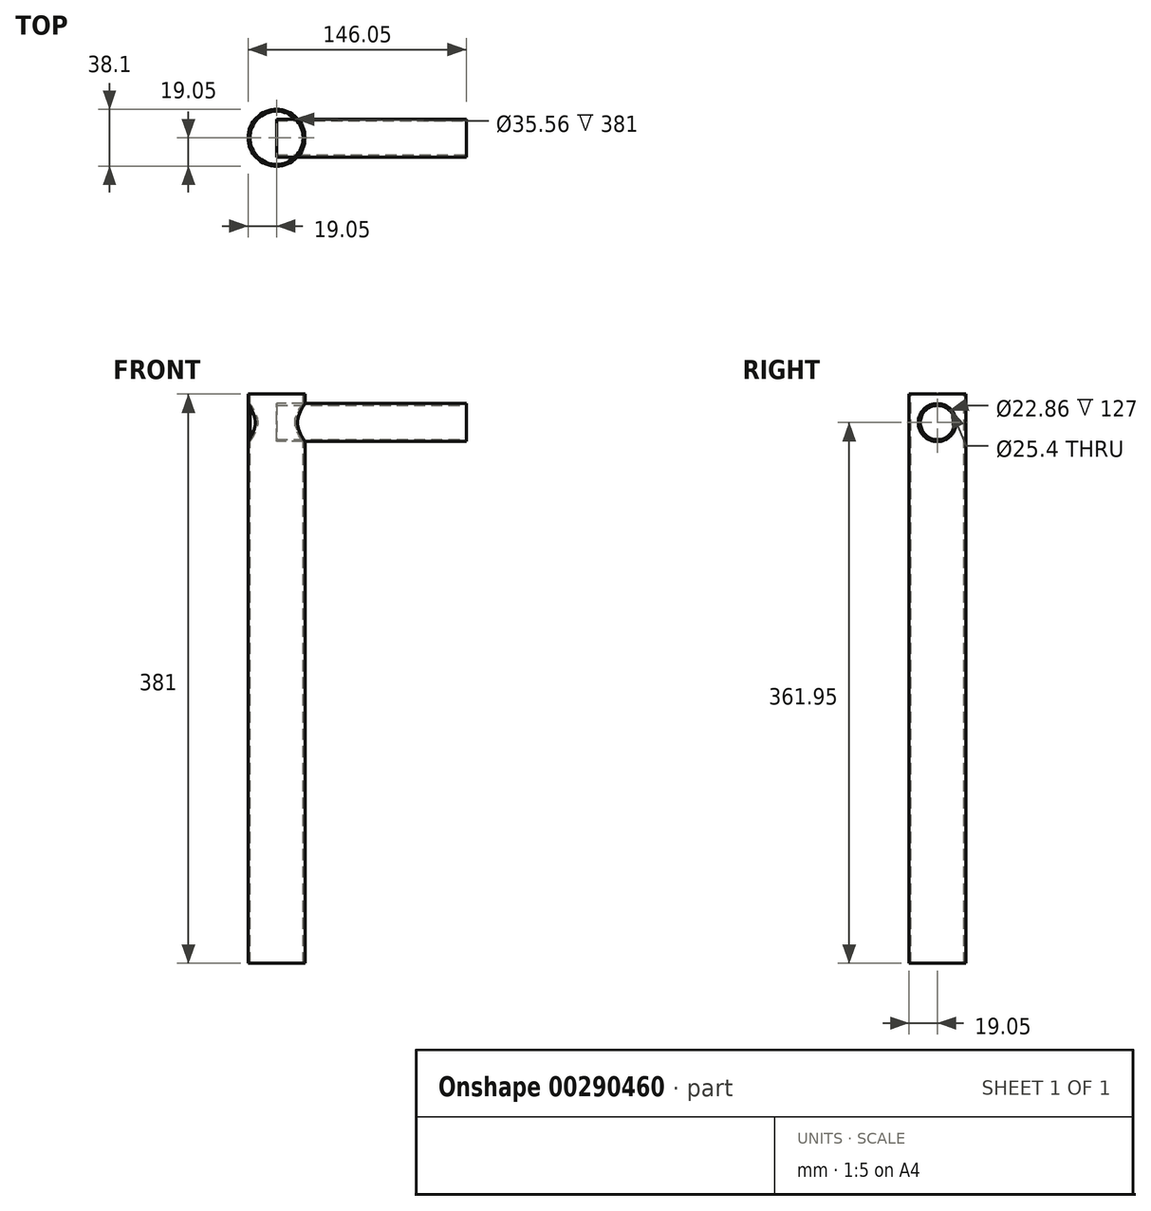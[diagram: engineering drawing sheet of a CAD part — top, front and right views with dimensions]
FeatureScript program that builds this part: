
annotation { "Feature Type Name" : "Feature", "Feature Type Description" : "" }
export const myFeature = defineFeature(function(context is Context, id is Id, definition is map)
    precondition{}
    {
        {
            var Q0;
            Q0=qCreatedBy(makeId("Top.planeOp"),FACE);
            var sketch = newSketch(context, id + "F0", { "sketchPlane" : qUnion([Q0])});
            skCircle(sketch, "E0", {"center": v(0, 0) * mm, "radius": 19.05 * mm});
            skSolve(sketch);
        }
        {
            var Q0;
            Q0 = qSketchRegion(id + "F0", true);
            extrude(context, id + "F1", {"entities" : qUnion([Q0]), "depth" : 381 * mm});
        }
        {
            var Q0;
            Q0=makeQuery(id+"F1.opExtrude","CAP_FACE",FACE,{"disambiguationData":[OSD([sQuery(id+"F0.wireOp",EDGE,"E0")])],"isStart":false});
            var sketch = newSketch(context, id + "F2", { "sketchPlane" : qUnion([Q0])});
            skCircle(sketch, "E1", {"center": v(0, 0) * mm, "radius": 17.78 * mm});
            skSolve(sketch);
        }
        {
            var Q0;
            Q0=makeQuery(id+"F2.imprint","IMPRINT",FACE,{"disambiguationData":[TD([[makeQuery(id+"F2.imprint","IMPRINT",EDGE,{"derivedFrom":sQuery(id+"F2.wireOp",EDGE,"E1")}),1.0]])]});
            extrude(context, id + "F3", {"entities" : qUnion([Q0]), "operationType" : NewBodyOperationType.REMOVE, "oppositeDirection" : true, "depth" : 381 * mm});
        }
        {
            var Q0;
            Q0=qCreatedBy(makeId("Right.planeOp"),FACE);
            var sketch = newSketch(context, id + "F4", { "sketchPlane" : qUnion([Q0])});
            skLineSegment(sketch, "E2", {"start": v(-19.19, 381) * mm, "end": v(-19.19, 342.9) * mm, "construction": true});
            skLineSegment(sketch, "E3", {"start": v(-19.19, 342.9) * mm, "end": v(18.91, 342.9) * mm, "construction": true});
            skLineSegment(sketch, "E4", {"start": v(18.91, 342.9) * mm, "end": v(18.91, 381) * mm, "construction": true});
            skLineSegment(sketch, "E5", {"start": v(18.91, 381) * mm, "end": v(-19.19, 381) * mm, "construction": true});
            skLineSegment(sketch, "E6", {"start": v(-19.19, 361.95) * mm, "end": v(18.91, 361.95) * mm, "construction": true});
            skCircle(sketch, "E7", {"center": v(-0.14, 361.95) * mm, "radius": 12.7 * mm});
            skSolve(sketch);
        }
        {
            var Q0;
            Q0 = qSketchRegion(id + "F4", true);
            extrude(context, id + "F5", {"entities" : qUnion([Q0]), "operationType" : NewBodyOperationType.ADD, "depth" : 127 * mm});
        }
        {
            var Q0;
            Q0=makeQuery(id+"F5.opExtrude","CAP_FACE",FACE,{"disambiguationData":[OSD([sQuery(id+"F4.wireOp",EDGE,"E7")])],"isStart":false});
            var sketch = newSketch(context, id + "F6", { "sketchPlane" : qUnion([Q0])});
            skLineSegment(sketch, "E8", {"start": v(0, 374.65) * mm, "end": v(0, 349.25) * mm, "construction": true});
            skLineSegment(sketch, "E9", {"start": v(0, 349.25) * mm, "end": v(0, 361.95) * mm, "construction": true});
            skLineSegment(sketch, "E10", {"start": v(0, 361.95) * mm, "end": v(12.56, 361.95) * mm, "construction": true});
            skLineSegment(sketch, "E11", {"start": v(12.56, 361.95) * mm, "end": v(-12.84, 361.95) * mm, "construction": true});
            skCircle(sketch, "E12", {"center": v(0, 361.95) * mm, "radius": 11.43 * mm});
            skSolve(sketch);
        }
        {
            var Q0;
            Q0=makeQuery(id+"F6.imprint","IMPRINT",FACE,{"disambiguationData":[TD([[makeQuery(id+"F6.imprint","IMPRINT",EDGE,{"derivedFrom":sQuery(id+"F6.wireOp",EDGE,"E12")}),1.0]])]});
            extrude(context, id + "F7", {"entities" : qUnion([Q0]), "operationType" : NewBodyOperationType.REMOVE, "oppositeDirection" : true, "depth" : 127 * mm});
        }
        {
            var Q0;
            Q0=qCreatedBy(makeId("Right.planeOp"),FACE);
            var sketch = newSketch(context, id + "F8", { "sketchPlane" : qUnion([Q0])});
            skLineSegment(sketch, "E13", {"start": v(19.05, 381) * mm, "end": v(-19.05, 381) * mm, "construction": true});
            skLineSegment(sketch, "E14", {"start": v(-19.05, 381) * mm, "end": v(-19.05, 342.9) * mm, "construction": true});
            skLineSegment(sketch, "E15", {"start": v(-19.05, 342.9) * mm, "end": v(19.05, 342.9) * mm, "construction": true});
            skLineSegment(sketch, "E16", {"start": v(19.05, 342.9) * mm, "end": v(19.05, 381) * mm, "construction": true});
            skLineSegment(sketch, "E17", {"start": v(19.05, 361.95) * mm, "end": v(-19.05, 361.95) * mm, "construction": true});
            skLineSegment(sketch, "E18", {"start": v(0, 381) * mm, "end": v(0, 342.9) * mm, "construction": true});
            skCircle(sketch, "E19", {"center": v(0, 361.95) * mm, "radius": 12.7 * mm});
            skSolve(sketch);
        }
        {
            var Q0;
            Q0 = qSketchRegion(id + "F8", true);
            extrude(context, id + "F9", {"entities" : qUnion([Q0]), "operationType" : NewBodyOperationType.REMOVE, "oppositeDirection" : true, "depth" : 25.4 * mm});
        }
    });
